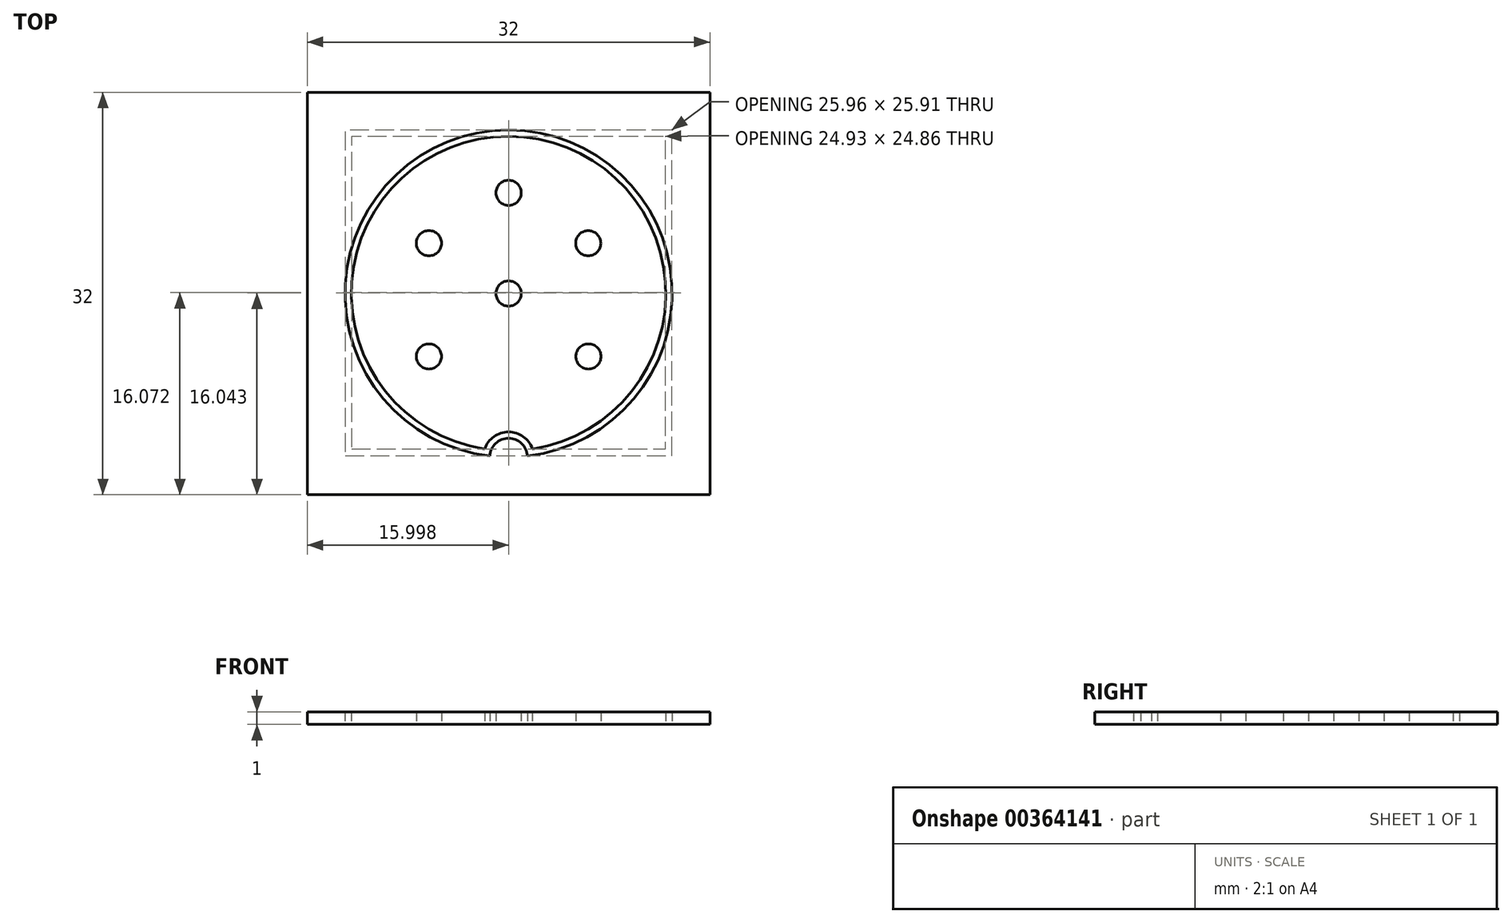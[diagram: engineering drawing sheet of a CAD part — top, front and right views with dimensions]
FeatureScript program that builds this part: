
annotation { "Feature Type Name" : "Feature", "Feature Type Description" : "" }
export const myFeature = defineFeature(function(context is Context, id is Id, definition is map)
    precondition{}
    {
        {
            var Q0;
            Q0=qCreatedBy(makeId("Top.planeOp"),FACE);
            var sketch = newSketch(context, id + "F0", { "sketchPlane" : qUnion([Q0])});
            skArc(sketch, "E0", {"start": v(1.9, -12.36) * mm, "mid": v(0, 12.5) * mm, "end": v(-1.9, -12.36) * mm});
            skCircle(sketch, "E1", {"center": v(0, 8) * mm, "radius": 1 * mm});
            skCircle(sketch, "E2", {"center": v(-6.33, 4) * mm, "radius": 1 * mm});
            skCircle(sketch, "E3", {"center": v(6.33, 4) * mm, "radius": 1 * mm});
            skArc(sketch, "E4", {"start": v(1.5, -12.91) * mm, "mid": v(0, 13) * mm, "end": v(-1.5, -12.91) * mm});
            skArc(sketch, "E5", {"start": v(1.5, -12.91) * mm, "mid": v(0, -11.5) * mm, "end": v(-1.5, -12.91) * mm});
            skArc(sketch, "E6", {"start": v(1.9, -12.36) * mm, "mid": v(0, -11) * mm, "end": v(-1.9, -12.36) * mm});
            skLineSegment(sketch, "E7.bottom", {"start": v(16, 16) * mm, "end": v(-16, 16) * mm});
            skLineSegment(sketch, "E7.top", {"start": v(16, -16) * mm, "end": v(-16, -16) * mm});
            skLineSegment(sketch, "E7.left", {"start": v(16, 16) * mm, "end": v(16, -16) * mm});
            skLineSegment(sketch, "E7.right", {"start": v(-16, 16) * mm, "end": v(-16, -16) * mm});
            skCircle(sketch, "E8", {"center": v(-6.33, -5) * mm, "radius": 1 * mm});
            skCircle(sketch, "E9", {"center": v(6.34, -5) * mm, "radius": 1 * mm});
            skCircle(sketch, "E10", {"center": v(0, 0) * mm, "radius": 1 * mm});
            skSolve(sketch);
        }
        {
            var Q0;
            Q0=makeQuery(id+"F0.imprint","IMPRINT",FACE,{"disambiguationData":[TD([[makeQuery(id+"F0.imprint","IMPRINT",EDGE,{"derivedFrom":sQuery(id+"F0.wireOp",EDGE,"E0")}),-1.0]])]});
            var Q1;
            Q1=makeQuery(id+"F0.imprint","IMPRINT",FACE,{"disambiguationData":[TD([[makeQuery(id+"F0.imprint","IMPRINT",EDGE,{"derivedFrom":sQuery(id+"F0.wireOp",EDGE,"E2")}),1.0]])]});
            var Q2;
            Q2=makeQuery(id+"F0.imprint","IMPRINT",FACE,{"disambiguationData":[TD([[makeQuery(id+"F0.imprint","IMPRINT",EDGE,{"derivedFrom":sQuery(id+"F0.wireOp",EDGE,"E1")}),1.0]])]});
            var Q3;
            Q3=makeQuery(id+"F0.imprint","IMPRINT",FACE,{"disambiguationData":[TD([[makeQuery(id+"F0.imprint","IMPRINT",EDGE,{"derivedFrom":sQuery(id+"F0.wireOp",EDGE,"E3")}),1.0]])]});
            var Q4;
            Q4=makeQuery(id+"F0.imprint","IMPRINT",FACE,{"disambiguationData":[TD([[makeQuery(id+"F0.imprint","IMPRINT",EDGE,{"derivedFrom":sQuery(id+"F0.wireOp",EDGE,"E10")}),1.0]])]});
            var Q5;
            Q5=makeQuery(id+"F0.imprint","IMPRINT",FACE,{"disambiguationData":[TD([[makeQuery(id+"F0.imprint","IMPRINT",EDGE,{"derivedFrom":sQuery(id+"F0.wireOp",EDGE,"E8")}),1.0]])]});
            var Q6;
            Q6=makeQuery(id+"F0.imprint","IMPRINT",FACE,{"disambiguationData":[TD([[makeQuery(id+"F0.imprint","IMPRINT",EDGE,{"derivedFrom":sQuery(id+"F0.wireOp",EDGE,"E9")}),1.0]])]});
            extrude(context, id + "F1", {"entities" : qUnion([Q0, Q1, Q2, Q3, Q4, Q5, Q6]), "depth" : 1 * mm});
        }
        {
            var Q0;
            Q0=makeQuery(id+"F0.imprint","IMPRINT",FACE,{"disambiguationData":[TD([[makeQuery(id+"F0.imprint","IMPRINT",EDGE,{"derivedFrom":sQuery(id+"F0.wireOp",EDGE,"E4")}),-1.0]])]});
            extrude(context, id + "F2", {"entities" : qUnion([Q0]), "depth" : 1 * mm});
        }
    });
